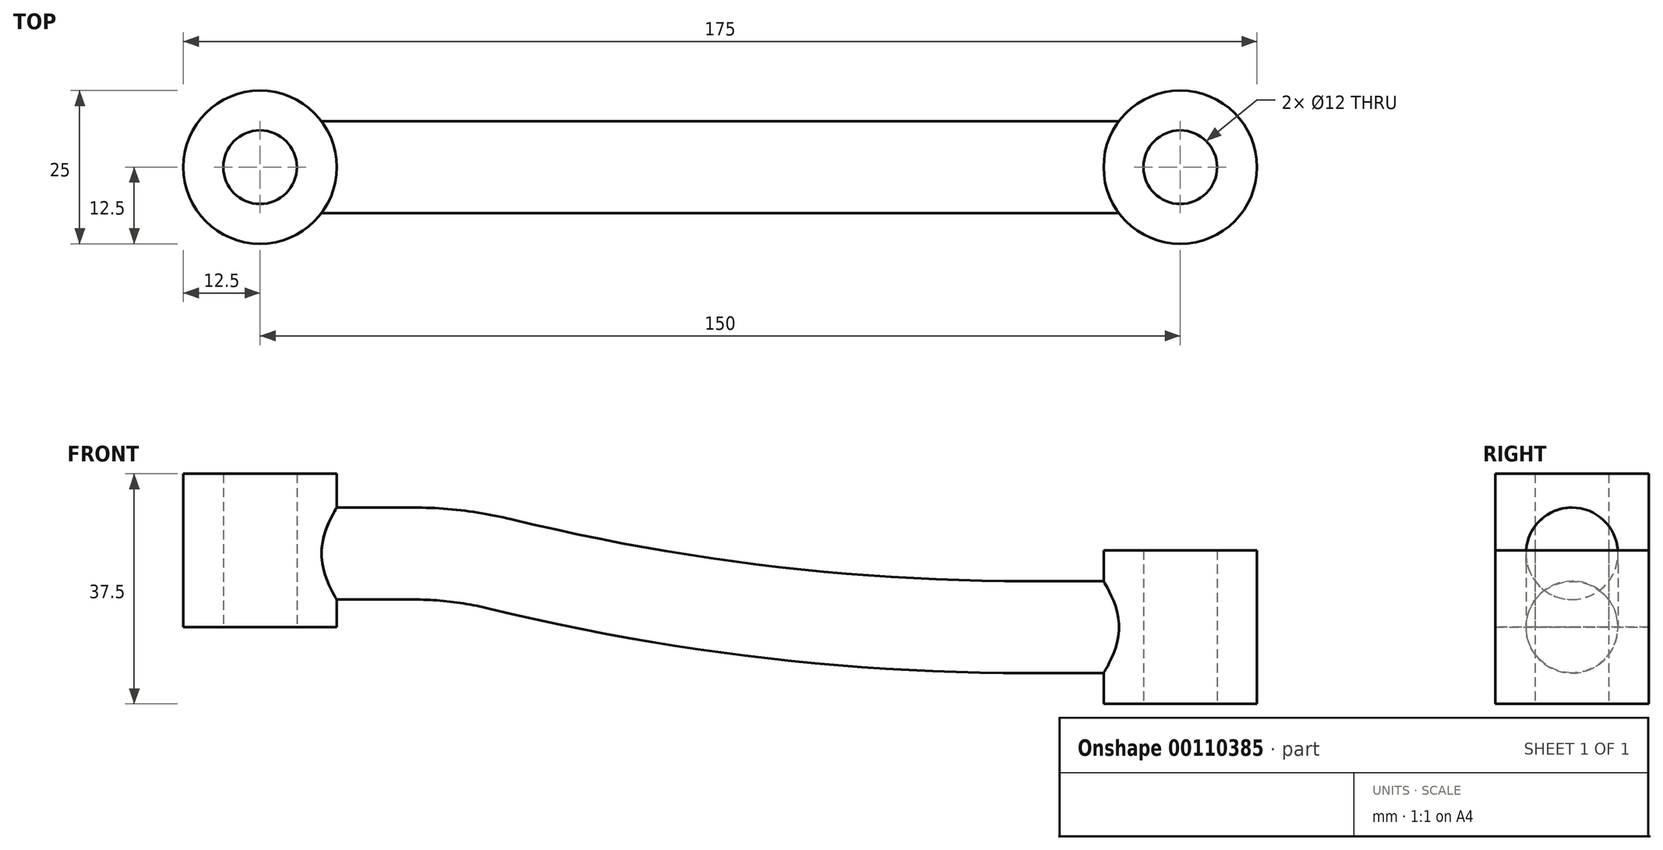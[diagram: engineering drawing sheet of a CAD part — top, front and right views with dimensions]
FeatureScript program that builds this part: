
annotation { "Feature Type Name" : "Feature", "Feature Type Description" : "" }
export const myFeature = defineFeature(function(context is Context, id is Id, definition is map)
    precondition{}
    {
        {
            var Q0;
            Q0=qCreatedBy(makeId("Front.planeOp"),FACE);
            var sketch = newSketch(context, id + "F0", { "sketchPlane" : qUnion([Q0])});
            skLineSegment(sketch, "E0", {"start": v(0, 12) * mm, "end": v(25, 12) * mm});
            skArc(sketch, "E1", {"start": v(39.2, 10.3) * mm, "mid": v(81.79, 2.58) * mm, "end": v(125, 0) * mm});
            skLineSegment(sketch, "E2", {"start": v(125, 0) * mm, "end": v(150, 0) * mm});
            skPoint(sketch, "E3.visualSharp", {"position": v(32.48, 12) * mm});
            skArc(sketch, "E3.filletArc", {"start": v(39.2, 10.3) * mm, "mid": v(32.15, 11.57) * mm, "end": v(25, 12) * mm});
            skSolve(sketch);
        }
        {
            var Q0;
            Q0=qCreatedBy(makeId("Right.planeOp"),FACE);
            var sketch = newSketch(context, id + "F1", { "sketchPlane" : qUnion([Q0])});
            skCircle(sketch, "E4", {"center": v(0, 12) * mm, "radius": 7.5 * mm});
            skSolve(sketch);
        }
        {
            var Q0;
            Q0=makeQuery(id+"F1.imprint","IMPRINT",FACE,{"disambiguationData":[TD([[makeQuery(id+"F1.imprint","IMPRINT",EDGE,{"derivedFrom":sQuery(id+"F1.wireOp",EDGE,"E4")}),1.0]])]});
            var Q1;
            Q1=sQuery(id+"F0.wireOp",EDGE,"E0");
            var Q2;
            Q2=sQuery(id+"F0.wireOp",EDGE,"E3.filletArc");
            var Q3;
            Q3=sQuery(id+"F0.wireOp",EDGE,"E1");
            var Q4;
            Q4=sQuery(id+"F0.wireOp",EDGE,"E2");
            sweep(context, id + "F2", {"profiles" : qUnion([Q0]), "path" : qUnion([Q1, Q2, Q3, Q4])});
        }
        {
            var Q0;
            Q0=qCreatedBy(makeId("Top.planeOp"),FACE);
            var sketch = newSketch(context, id + "F3", { "sketchPlane" : qUnion([Q0])});
            skCircle(sketch, "E5", {"center": v(0, 0) * mm, "radius": 12.5 * mm});
            skCircle(sketch, "E6", {"center": v(150, 0) * mm, "radius": 12.5 * mm});
            skCircle(sketch, "E7", {"center": v(0, 0) * mm, "radius": 6 * mm});
            skCircle(sketch, "E8", {"center": v(150, 0) * mm, "radius": 6 * mm});
            skSolve(sketch);
        }
        {
            var Q0;
            Q0=makeQuery(id+"F3.imprint","IMPRINT",FACE,{"disambiguationData":[TD([[makeQuery(id+"F3.imprint","IMPRINT",EDGE,{"derivedFrom":sQuery(id+"F3.wireOp",EDGE,"E5")}),1.0]])]});
            var Q1;
            Q1=sQuery(id+"F3.wireOp",EDGE,"E5");
            extrude(context, id + "F4", {"entities" : qUnion([Q0]), "operationType" : NewBodyOperationType.ADD, "surfaceEntities" : qUnion([Q1]), "depth" : 25 * mm});
        }
        {
            var Q0;
            Q0=makeQuery(id+"F3.imprint","IMPRINT",FACE,{"disambiguationData":[TD([[makeQuery(id+"F3.imprint","IMPRINT",EDGE,{"derivedFrom":sQuery(id+"F3.wireOp",EDGE,"E6")}),1.0]])]});
            extrude(context, id + "F5", {"entities" : qUnion([Q0]), "operationType" : NewBodyOperationType.ADD, "endBound" : BoundingType.SYMMETRIC, "depth" : 25 * mm});
        }
        {
            var Q0;
            Q0=makeQuery(id+"F3.imprint","IMPRINT",FACE,{"disambiguationData":[TD([[makeQuery(id+"F3.imprint","IMPRINT",EDGE,{"derivedFrom":sQuery(id+"F3.wireOp",EDGE,"E5")}),1.0]])]});
            var sketch = newSketch(context, id + "F6", { "sketchPlane" : qUnion([Q0])});
            skCircle(sketch, "E9.0", {"center": v(0, 0) * mm, "radius": 6 * mm});
            skSolve(sketch);
        }
        {
            var Q0;
            Q0 = qSketchRegion(id + "F6", true);
            extrude(context, id + "F7", {"entities" : qUnion([Q0]), "operationType" : NewBodyOperationType.REMOVE, "endBound" : BoundingType.THROUGH_ALL, "depth" : 25 * mm});
        }
        {
            var Q0;
            Q0=makeQuery(id+"F3.imprint","IMPRINT",FACE,{"disambiguationData":[TD([[makeQuery(id+"F3.imprint","IMPRINT",EDGE,{"derivedFrom":sQuery(id+"F3.wireOp",EDGE,"E8")}),1.0]])]});
            var sketch = newSketch(context, id + "F8", { "sketchPlane" : qUnion([Q0])});
            skCircle(sketch, "E10.0", {"center": v(150, 0) * mm, "radius": 6 * mm});
            skSolve(sketch);
        }
        {
            var Q0;
            Q0 = qSketchRegion(id + "F8", true);
            extrude(context, id + "F9", {"entities" : qUnion([Q0]), "operationType" : NewBodyOperationType.REMOVE, "endBound" : BoundingType.THROUGH_ALL, "oppositeDirection" : true, "depth" : 25 * mm, "hasSecondDirection" : true, "secondDirectionBound" : SecondDirectionBoundingType.THROUGH_ALL, "secondDirectionOppositeDirection" : false, "secondDirectionDepth" : 25 * mm});
        }
    });
